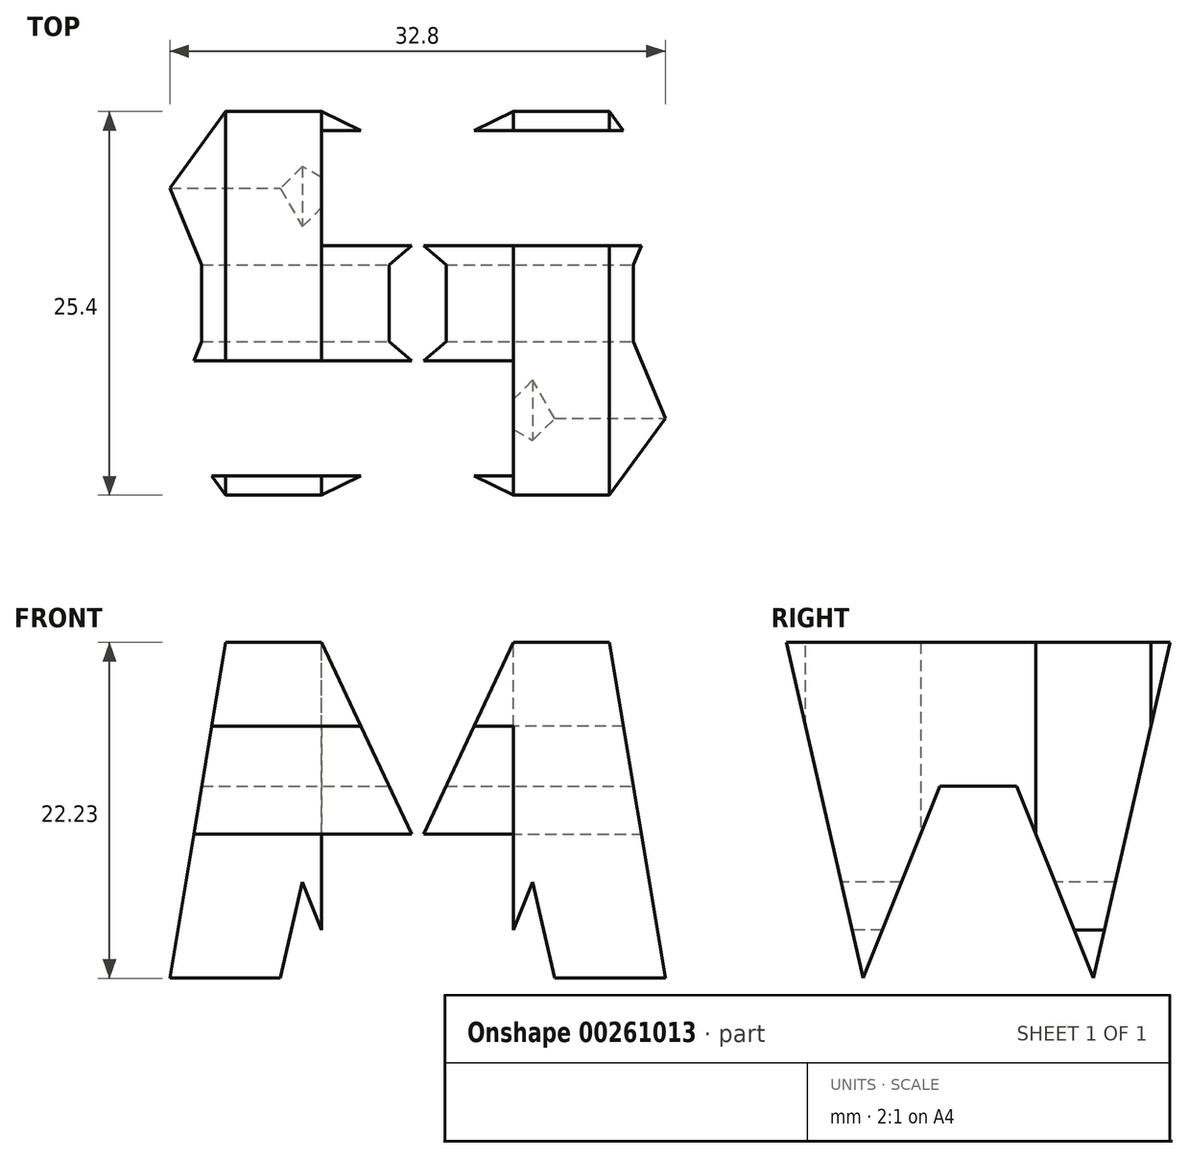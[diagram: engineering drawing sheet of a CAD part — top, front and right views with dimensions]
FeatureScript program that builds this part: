
annotation { "Feature Type Name" : "Feature", "Feature Type Description" : "" }
export const myFeature = defineFeature(function(context is Context, id is Id, definition is map)
    precondition{}
    {
        {
            var Q0;
            Q0=qCreatedBy(makeId("Front.planeOp"),FACE);
            var sketch = newSketch(context, id + "F0", { "sketchPlane" : qUnion([Q0])});
            skLineSegment(sketch, "E0", {"start": v(0, 0) * mm, "end": v(0, 38.1) * mm});
            skLineSegment(sketch, "E1", {"start": v(0, 38.1) * mm, "end": v(38.1, 38.1) * mm});
            skLineSegment(sketch, "E2", {"start": v(38.1, 38.1) * mm, "end": v(38.1, 0) * mm});
            skLineSegment(sketch, "E3", {"start": v(0, 0) * mm, "end": v(38.1, 0) * mm});
            skSolve(sketch);
        }
        {
            var Q0;
            Q0=makeQuery(id+"F0.imprint","IMPRINT",FACE,{"disambiguationData":[TD([[makeQuery(id+"F0.imprint","IMPRINT",EDGE,{"derivedFrom":sQuery(id+"F0.wireOp",EDGE,"E0")}),-1.0]])]});
            extrude(context, id + "F1", {"entities" : qUnion([Q0]), "depth" : 38.1 * mm});
        }
        {
            var Q0;
            Q0=qCreatedBy(makeId("Front.planeOp"),FACE);
            cPlane(context, id + "F2", {"entities" : qUnion([Q0]), "cplaneType" : CPlaneType.OFFSET, "offset" : 38.1 * mm, "width" : 152.4 * mm, "height" : 152.4 * mm});
        }
        {
            var Q0;
            Q0=qCreatedBy(makeId("Right.planeOp"),FACE);
            cPlane(context, id + "F3", {"entities" : qUnion([Q0]), "cplaneType" : CPlaneType.OFFSET, "offset" : 38.1 * mm, "width" : 152.4 * mm, "height" : 152.4 * mm});
        }
        {
            var Q0;
            Q0=qCreatedBy(makeId("Top.planeOp"),FACE);
            cPlane(context, id + "F4", {"entities" : qUnion([Q0]), "cplaneType" : CPlaneType.OFFSET, "offset" : 38.1 * mm, "width" : 152.4 * mm, "height" : 152.4 * mm});
        }
        {
            var Q0;
            Q0=qCreatedBy(id+"F3.planeOp",FACE);
            var sketch = newSketch(context, id + "F5", { "sketchPlane" : qUnion([Q0])});
            skLineSegment(sketch, "E4", {"start": v(0, 0) * mm, "end": v(0, 38.1) * mm});
            skLineSegment(sketch, "E5", {"start": v(-38.1, 38.1) * mm, "end": v(0, 38.1) * mm});
            skLineSegment(sketch, "E6", {"start": v(-38.1, 38.1) * mm, "end": v(-38.1, 0) * mm});
            skLineSegment(sketch, "E7", {"start": v(0, 0) * mm, "end": v(-38.1, 0) * mm});
            skLineSegment(sketch, "E8", {"start": v(-38.1, 38.1) * mm, "end": v(-31.75, 0) * mm});
            skLineSegment(sketch, "E9", {"start": v(-31.75, 0) * mm, "end": v(-25.4, 0) * mm});
            skLineSegment(sketch, "E10", {"start": v(-25.4, 0) * mm, "end": v(-19.05, 15.88) * mm});
            skLineSegment(sketch, "E11", {"start": v(-19.05, 15.88) * mm, "end": v(-12.7, 0) * mm});
            skLineSegment(sketch, "E12", {"start": v(-12.7, 0) * mm, "end": v(-6.35, 0) * mm});
            skLineSegment(sketch, "E13", {"start": v(-6.35, 0) * mm, "end": v(0, 38.1) * mm});
            skLineSegment(sketch, "E14", {"start": v(-6.35, 38.1) * mm, "end": v(-11.43, 15.87) * mm});
            skLineSegment(sketch, "E15", {"start": v(-11.43, 15.88) * mm, "end": v(-16.51, 28.58) * mm});
            skLineSegment(sketch, "E16", {"start": v(-16.51, 28.58) * mm, "end": v(-21.6, 28.58) * mm});
            skLineSegment(sketch, "E17", {"start": v(-21.6, 28.58) * mm, "end": v(-26.67, 15.88) * mm});
            skLineSegment(sketch, "E18", {"start": v(-26.67, 15.88) * mm, "end": v(-31.75, 38.1) * mm});
            skLineSegment(sketch, "E19", {"start": v(-31.75, 38.1) * mm, "end": v(-38.1, 38.1) * mm});
            skLineSegment(sketch, "E20", {"start": v(-6.35, 38.1) * mm, "end": v(0, 38.1) * mm});
            skSolve(sketch);
        }
        {
            var Q0;
            Q0=makeQuery(id+"F5.imprint","IMPRINT",FACE,{"disambiguationData":[TD([[makeQuery(id+"F5.imprint","IMPRINT",EDGE,{"derivedFrom":sQuery(id+"F5.wireOp",EDGE,"E5")}),-1.0]])]});
            var Q1;
            {var subQ0=sQuery(id+"F5.wireOp",EDGE,"E6");Q1=makeQuery(id+"F5.imprint","IMPRINT",FACE,{"disambiguationData":[TD([[makeQuery(id+"F5.imprint","IMPRINT",EDGE,{"derivedFrom":subQ0}),1.0]])]});}
            var Q2;
            {var subQ0=sQuery(id+"F5.wireOp",EDGE,"E4");Q2=makeQuery(id+"F5.imprint","IMPRINT",FACE,{"disambiguationData":[TD([[makeQuery(id+"F5.imprint","IMPRINT",EDGE,{"derivedFrom":subQ0}),1.0]])]});}
            var Q3;
            {var subQ0=sQuery(id+"F5.wireOp",EDGE,"E10");Q3=makeQuery(id+"F5.imprint","IMPRINT",FACE,{"disambiguationData":[TD([[makeQuery(id+"F5.imprint","IMPRINT",EDGE,{"derivedFrom":subQ0}),-1.0]])]});}
            extrude(context, id + "F6", {"entities" : qUnion([Q0, Q1, Q2, Q3]), "operationType" : NewBodyOperationType.REMOVE, "oppositeDirection" : true, "depth" : 38.1 * mm});
        }
        {
            var Q0;
            Q0=qCreatedBy(id+"F2.planeOp",FACE);
            var sketch = newSketch(context, id + "F7", { "sketchPlane" : qUnion([Q0])});
            skLineSegment(sketch, "E21", {"start": v(0, 0) * mm, "end": v(38.1, 0) * mm});
            skLineSegment(sketch, "E22", {"start": v(38.1, 0) * mm, "end": v(38.1, 38.1) * mm});
            skLineSegment(sketch, "E23", {"start": v(38.1, 38.1) * mm, "end": v(0, 38.1) * mm});
            skLineSegment(sketch, "E24", {"start": v(0, 38.1) * mm, "end": v(0, 0) * mm});
            skLineSegment(sketch, "E25", {"start": v(0, 0) * mm, "end": v(6.35, 38.1) * mm});
            skLineSegment(sketch, "E26", {"start": v(6.35, 38.1) * mm, "end": v(12.7, 38.1) * mm});
            skLineSegment(sketch, "E27", {"start": v(12.7, 38.1) * mm, "end": v(19.05, 24.55) * mm});
            skLineSegment(sketch, "E28", {"start": v(19.05, 24.55) * mm, "end": v(25.4, 38.1) * mm});
            skLineSegment(sketch, "E29", {"start": v(25.4, 38.1) * mm, "end": v(31.75, 38.1) * mm});
            skLineSegment(sketch, "E30", {"start": v(31.75, 38.1) * mm, "end": v(38.1, 0) * mm});
            skLineSegment(sketch, "E31", {"start": v(31.75, 0) * mm, "end": v(26.67, 22.23) * mm});
            skLineSegment(sketch, "E32", {"start": v(26.67, 22.23) * mm, "end": v(21.59, 9.53) * mm});
            skLineSegment(sketch, "E33", {"start": v(21.59, 9.53) * mm, "end": v(16.51, 9.53) * mm});
            skLineSegment(sketch, "E34", {"start": v(16.51, 9.53) * mm, "end": v(11.43, 22.23) * mm});
            skLineSegment(sketch, "E35", {"start": v(11.43, 22.23) * mm, "end": v(6.35, 0) * mm});
            skLineSegment(sketch, "E36", {"start": v(6.35, 0) * mm, "end": v(0, 0) * mm});
            skSolve(sketch);
        }
        {
            var Q0;
            {var subQ0=sQuery(id+"F7.wireOp",EDGE,"E27");Q0=makeQuery(id+"F7.imprint","IMPRINT",FACE,{"disambiguationData":[TD([[makeQuery(id+"F7.imprint","IMPRINT",EDGE,{"derivedFrom":subQ0}),1.0]])]});}
            var Q1;
            {var subQ2=sQuery(id+"F7.wireOp",EDGE,"E31");Q1=makeQuery(id+"F7.imprint","IMPRINT",FACE,{"disambiguationData":[TD([[makeQuery(id+"F7.imprint","IMPRINT",EDGE,{"derivedFrom":subQ2}),1.0]])]});}
            var Q2;
            {var subQ0=sQuery(id+"F7.wireOp",EDGE,"E22");Q2=makeQuery(id+"F7.imprint","IMPRINT",FACE,{"disambiguationData":[TD([[makeQuery(id+"F7.imprint","IMPRINT",EDGE,{"derivedFrom":subQ0}),1.0]])]});}
            var Q3;
            {var subQ0=sQuery(id+"F7.wireOp",EDGE,"E24");Q3=makeQuery(id+"F7.imprint","IMPRINT",FACE,{"disambiguationData":[TD([[makeQuery(id+"F7.imprint","IMPRINT",EDGE,{"derivedFrom":subQ0}),1.0]])]});}
            extrude(context, id + "F8", {"entities" : qUnion([Q0, Q1, Q2, Q3]), "operationType" : NewBodyOperationType.REMOVE, "oppositeDirection" : true, "depth" : 38.1 * mm});
        }
        {
            var Q0;
            Q0=qCreatedBy(id+"F4.planeOp",FACE);
            var sketch = newSketch(context, id + "F9", { "sketchPlane" : qUnion([Q0])});
            skLineSegment(sketch, "E37", {"start": v(0, 0) * mm, "end": v(38.1, 0) * mm});
            skLineSegment(sketch, "E38", {"start": v(38.1, 0) * mm, "end": v(38.1, -38.1) * mm});
            skLineSegment(sketch, "E39", {"start": v(38.1, -38.1) * mm, "end": v(0, -38.1) * mm});
            skLineSegment(sketch, "E40", {"start": v(0, -38.1) * mm, "end": v(0, 0) * mm});
            skLineSegment(sketch, "E41", {"start": v(38.1, -7.62) * mm, "end": v(12.7, -7.62) * mm});
            skLineSegment(sketch, "E42", {"start": v(12.7, -7.62) * mm, "end": v(12.7, -15.24) * mm});
            skLineSegment(sketch, "E43", {"start": v(12.7, -15.24) * mm, "end": v(38.1, -15.24) * mm});
            skLineSegment(sketch, "E44", {"start": v(0, -22.86) * mm, "end": v(25.4, -22.86) * mm});
            skLineSegment(sketch, "E45", {"start": v(25.4, -22.86) * mm, "end": v(25.4, -30.48) * mm});
            skLineSegment(sketch, "E46", {"start": v(25.4, -30.48) * mm, "end": v(0, -30.48) * mm});
            skLineSegment(sketch, "E47", {"start": v(0, -30.48) * mm, "end": v(0, -22.86) * mm});
            skLineSegment(sketch, "E48", {"start": v(38.1, -15.24) * mm, "end": v(38.1, -7.62) * mm});
            skSolve(sketch);
        }
        {
            var Q0;
            Q0=makeQuery(id+"F9.imprint","IMPRINT",FACE,{"disambiguationData":[TD([[makeQuery(id+"F9.imprint","IMPRINT",EDGE,{"derivedFrom":sQuery(id+"F9.wireOp",EDGE,"E41")}),1.0]])]});
            var Q1;
            Q1=makeQuery(id+"F9.imprint","IMPRINT",FACE,{"disambiguationData":[TD([[makeQuery(id+"F9.imprint","IMPRINT",EDGE,{"derivedFrom":sQuery(id+"F9.wireOp",EDGE,"E44")}),-1.0]])]});
            extrude(context, id + "F10", {"entities" : qUnion([Q0, Q1]), "operationType" : NewBodyOperationType.REMOVE, "oppositeDirection" : true, "depth" : 38.1 * mm});
        }
    });
